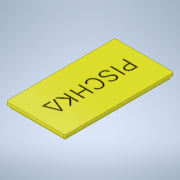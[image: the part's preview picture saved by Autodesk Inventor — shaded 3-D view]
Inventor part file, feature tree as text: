
AUTODESK INVENTOR PART (.ipt)
format: ipt  version: 2020.1 (Build 241239000, 239)  size: 468,992 bytes
history: native  units: mm
features: sketch x3, extrude x2, other x1, emboss x1
ambient origin geometry x8: Origin, YZ Plane, XZ Plane, XY Plane, X Axis, Y Axis, Z Axis, Center Point
bodies: Body1 (feature_tree)
feature tree (7):
  other  "Receiver Case.ipt"
  sketch  "Sketch3"  dims[d9=2.0mm d10=0.0mm d11=2.0mm d12=0.0mm]
  extrude  "Extrusion3"  Depth=0.4mm
  extrude  "Extrusion4"  Depth=2.0mm TaperAngle=0.0deg
  emboss  "Emboss1"
  sketch  "Sketch1_1"  dims[d0=10.0mm d8=0.4mm]
  sketch  "Sketch4"  dims[d13=0.4mm d14=0.0mm d15=0.15mm d16=0.15mm d17=0.15mm d18=0.15mm d19=0.8mm]
